annotation { "Feature Type Name" : "Feature", "Feature Type Description" : "" }
export const myFeature = defineFeature(function(context is Context, id is Id, definition is map)
    precondition{}
    {
        {
            var Q0;
            Q0=qCreatedBy(makeId("Top.planeOp"),FACE);
            var sketch = newSketch(context, id + "F0", { "sketchPlane" : qUnion([Q0])});
            skCircle(sketch, "E0", {"center": v(-3.44, 20.55) * mm, "radius": 2.25 * mm});
            skPoint(sketch, "E1.start.orphan", {"position": v(0, 19.88) * mm});
            skArc(sketch, "E2", {"start": v(11.02, -22.89) * mm, "mid": v(0, 25.4) * mm, "end": v(-11.02, -22.89) * mm});
            skLineSegment(sketch, "E3.bottom", {"start": v(-22.14, -22.89) * mm, "end": v(-11.02, -22.89) * mm});
            skLineSegment(sketch, "E3.top", {"start": v(-22.14, -41.12) * mm, "end": v(23.07, -41.12) * mm});
            skLineSegment(sketch, "E3.left", {"start": v(-22.14, -22.89) * mm, "end": v(-22.14, -41.12) * mm});
            skLineSegment(sketch, "E3.right", {"start": v(23.07, -22.89) * mm, "end": v(23.07, -41.12) * mm});
            skLineSegment(sketch, "E4.trimOffspring", {"start": v(11.02, -22.89) * mm, "end": v(23.07, -22.89) * mm});
            skSolve(sketch);
        }
        {
            var Q0;
            Q0=qCreatedBy(makeId("Top.planeOp"),FACE);
            var sketch = newSketch(context, id + "F1", { "sketchPlane" : qUnion([Q0])});
            skArc(sketch, "E5.trimOffspring", {"start": v(24.62, 4.23) * mm, "mid": v(15.16, 16.49) * mm, "end": v(0.08, 20.03) * mm});
            skArc(sketch, "E6", {"start": v(20.4, -14.41) * mm, "mid": v(15.47, 4.6) * mm, "end": v(-2.84, 11.72) * mm});
            skArc(sketch, "E7.trimOffspring", {"start": v(11.23, -22.31) * mm, "mid": v(12.24, -17.76) * mm, "end": v(12.01, -13.11) * mm});
            skArc(sketch, "E8.trimOffspring", {"start": v(4.55, 24.56) * mm, "mid": v(-3.22, 13.64) * mm, "end": v(0.84, 0.87) * mm});
            skArc(sketch, "E9", {"start": v(-6.91, 24) * mm, "mid": v(-10.9, 8.7) * mm, "end": v(-2.38, -4.62) * mm});
            skArc(sketch, "E10.trimOffspring", {"start": v(-17.01, 18.28) * mm, "mid": v(-19.48, 2.54) * mm, "end": v(-8.34, -8.86) * mm});
            skArc(sketch, "E11", {"start": v(-12.4, -21.68) * mm, "mid": v(1.3, -21.63) * mm, "end": v(12.01, -13.11) * mm});
            skArc(sketch, "E12.0", {"start": v(-7.74, 23.75) * mm, "mid": v(-11.36, 8.3) * mm, "end": v(-2.73, -5) * mm});
            skArc(sketch, "E13.0", {"start": v(-18.65, 16.61) * mm, "mid": v(-19.68, 1.57) * mm, "end": v(-9.06, -9.14) * mm});
            skArc(sketch, "E14.0", {"start": v(23.81, 7.53) * mm, "mid": v(14.19, 17.66) * mm, "end": v(0.52, 20.59) * mm});
            skArc(sketch, "E15.0", {"start": v(21.13, -13.32) * mm, "mid": v(15.46, 5.36) * mm, "end": v(-2.82, 12.23) * mm});
            skArc(sketch, "E16.0", {"start": v(-22.73, -10.35) * mm, "mid": v(-5.68, -17.15) * mm, "end": v(9.75, -7.22) * mm});
            skArc(sketch, "E17.0", {"start": v(11.89, -21.97) * mm, "mid": v(11.5, -9.54) * mm, "end": v(3.1, -0.36) * mm});
            skArc(sketch, "E18.0", {"start": v(-23.92, -7.18) * mm, "mid": v(-16.73, -9.96) * mm, "end": v(-9.06, -9.14) * mm});
            skArc(sketch, "E19.trimOffspring", {"start": v(-8.34, -8.86) * mm, "mid": v(-5.33, -7.23) * mm, "end": v(-2.73, -5) * mm});
            skArc(sketch, "E20.trimOffspring", {"start": v(-2.38, -4.62) * mm, "mid": v(-0.5, -2.03) * mm, "end": v(0.84, 0.87) * mm});
            skArc(sketch, "E21.0", {"start": v(5.44, 24.38) * mm, "mid": v(-2.78, 12.67) * mm, "end": v(3.1, -0.36) * mm});
            skPoint(sketch, "E22.orphan", {"position": v(1.05, 0) * mm});
            skPoint(sketch, "E23.orphan", {"position": v(0, 20.02) * mm});
            skArc(sketch, "E24.trimOffspring", {"start": v(11.86, -12.4) * mm, "mid": v(11.12, -9.99) * mm, "end": v(10.05, -7.72) * mm});
            skArc(sketch, "E25.trimOffspring", {"start": v(9.75, -7.22) * mm, "mid": v(6.63, -3.43) * mm, "end": v(2.57, -0.66) * mm});
            skArc(sketch, "E26.trimOffspring", {"start": v(1.24, 0.48) * mm, "mid": v(1.89, -0.11) * mm, "end": v(2.57, -0.66) * mm});
            skArc(sketch, "E27", {"start": v(-14.78, -20.13) * mm, "mid": v(0.06, -21.49) * mm, "end": v(11.86, -12.39) * mm});
            skArc(sketch, "E28", {"start": v(-23.68, -7.95) * mm, "mid": v(-9.2, -9.73) * mm, "end": v(1.24, 0.48) * mm});
            skArc(sketch, "E29.0", {"start": v(-21.95, -11.91) * mm, "mid": v(-4.93, -17.57) * mm, "end": v(10.05, -7.72) * mm});
            skCircle(sketch, "E30", {"center": v(0, 0) * mm, "radius": 25.48 * mm});
            skArc(sketch, "E31.0", {"start": v(-18.65, 16.61) * mm, "mid": v(-24.38, 5.4) * mm, "end": v(-23.92, -7.18) * mm});
            skArc(sketch, "E32.trimOffspring", {"start": v(-7.74, 23.75) * mm, "mid": v(-12.68, 21.52) * mm, "end": v(-17.01, 18.28) * mm});
            skArc(sketch, "E33.trimOffspring", {"start": v(4.55, 24.56) * mm, "mid": v(-1.21, 24.95) * mm, "end": v(-6.91, 24) * mm});
            skArc(sketch, "E34.trimOffspring", {"start": v(-23.68, -7.95) * mm, "mid": v(-23.24, -9.16) * mm, "end": v(-22.73, -10.35) * mm});
            skArc(sketch, "E35.trimOffspring", {"start": v(-21.95, -11.91) * mm, "mid": v(-18.82, -16.42) * mm, "end": v(-14.78, -20.13) * mm});
            skArc(sketch, "E36.trimOffspring", {"start": v(23.81, 7.53) * mm, "mid": v(16.88, 18.41) * mm, "end": v(5.44, 24.38) * mm});
            skArc(sketch, "E37.trimOffspring", {"start": v(21.13, -13.32) * mm, "mid": v(24.5, -4.87) * mm, "end": v(24.62, 4.23) * mm});
            skArc(sketch, "E38.trimOffspring", {"start": v(11.89, -21.97) * mm, "mid": v(16.58, -18.68) * mm, "end": v(20.4, -14.41) * mm});
            skArc(sketch, "E39.trimOffspring", {"start": v(-12.4, -21.68) * mm, "mid": v(-0.66, -24.97) * mm, "end": v(11.23, -22.31) * mm});
            skSolve(sketch);
        }
        {
            var Q0;
            Q0=qCreatedBy(makeId("Top.planeOp"),FACE);
            var sketch = newSketch(context, id + "F2", { "sketchPlane" : qUnion([Q0])});
            skText(sketch, "E40", { "text": "11.30.15", "fontName": "OpenSans-BoldItalic.ttf"});
            skText(sketch, "E41", { "text": "Kylie Hock", "fontName": "OpenSans-Italic.ttf"});
            const initialGuessF2  = {"E40": [-0.00785, -0.0322, 1, 0, 0.00355], "E41": [-0.01321, -0.0388, 1, 0, 0.00402]};
            skSetInitialGuess(sketch, initialGuessF2);
            skSolve(sketch);
        }
        {
            var Q0;
            Q0 = qSketchRegion(id + "F0", true);
            extrude(context, id + "F3", {"entities" : qUnion([Q0]), "depth" : 5.08 * mm, "offsetDistance" : 25.4 * mm});
        }
        {
            var Q0;
            Q0 = qSketchRegion(id + "F2", true);
            extrude(context, id + "F4", {"entities" : qUnion([Q0]), "operationType" : NewBodyOperationType.ADD, "depth" : 6.38 * mm, "offsetDistance" : 25.4 * mm});
        }
        {
            var Q0;
            Q0 = qSketchRegion(id + "F1", true);
            extrude(context, id + "F5", {"entities" : qUnion([Q0]), "operationType" : NewBodyOperationType.ADD, "depth" : 6.02 * mm, "offsetDistance" : 25.4 * mm});
        }
    });